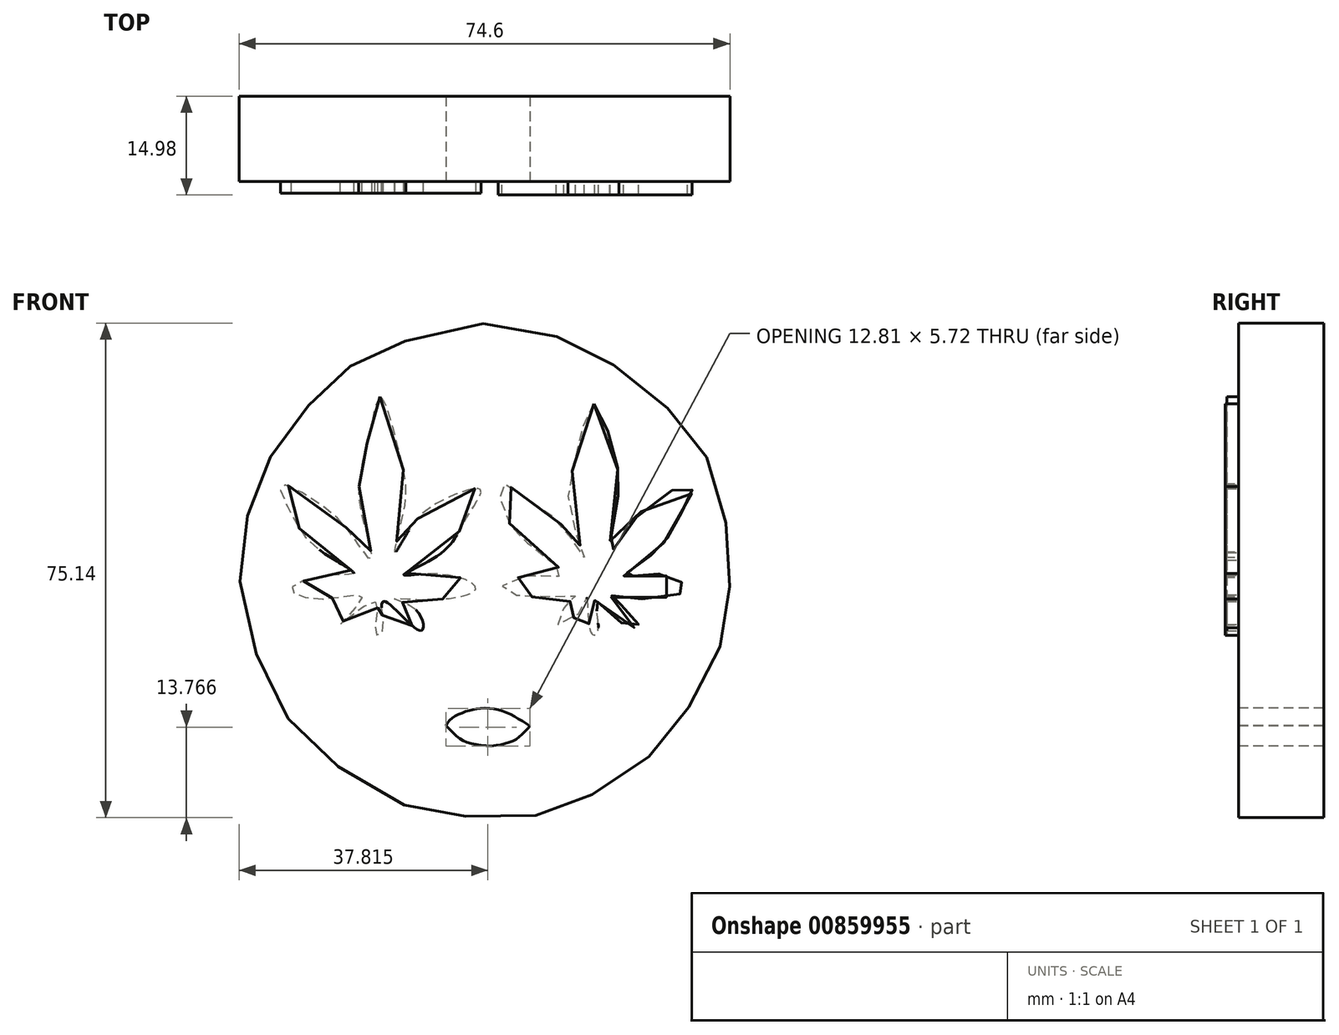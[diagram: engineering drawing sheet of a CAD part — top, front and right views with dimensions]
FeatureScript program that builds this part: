
annotation { "Feature Type Name" : "Feature", "Feature Type Description" : "" }
export const myFeature = defineFeature(function(context is Context, id is Id, definition is map)
    precondition{}
    {
        {
            var Q0;
            Q0=qCreatedBy(makeId("Front.planeOp"),FACE);
            var sketch = newSketch(context, id + "F0", { "sketchPlane" : qUnion([Q0])});
            skFitSpline(sketch, "E0", {"points": [v(-16.7, 29.13) * mm, v(-18.02, 24.43) * mm, v(-18.7, 21.9) * mm, v(-19.39, 19.04) * mm, v(-19.81, 15.55) * mm, v(-19.7, 12.33) * mm, v(-17.93, 4.31) * mm, v(-20.61, 7.65) * mm, v(-24.87, 12.13) * mm, v(-31.65, 15.66) * mm, v(-29.95, 10.92) * mm, v(-26.19, 6.08) * mm, v(-20.59, 2.33) * mm, v(-23.31, 2.06) * mm, v(-30.1, 0) * mm, v(-25.23, -1.6) * mm, v(-19.43, -1.4) * mm, v(-22.7, -5.46) * mm, v(-17.36, -2.02) * mm, v(-17.36, -6.82) * mm, v(-16.34, -6.78) * mm, v(-16.33, -2.15) * mm, v(-14.42, -3.11) * mm, v(-10.37, -6.4) * mm, v(-11, -3.5) * mm, v(-14.47, -1.57) * mm, v(-8.15, -1.69) * mm, v(-2.09, 0) * mm, v(-7.1, 2.12) * mm, v(-13.07, 2.08) * mm, v(-7.55, 5.2) * mm, v(-3.32, 11) * mm, v(-1.42, 15.02) * mm, v(-6.66, 13.63) * mm, v(-11.8, 9.5) * mm, v(-14.39, 5.47) * mm, v(-12.93, 12.38) * mm, v(-13.54, 19.91) * mm, v(-16.7, 29.13) * mm]});
            skSolve(sketch);
        }
        {
            var Q0;
            Q0 = qSketchRegion(id + "F0", true);
            extrude(context, id + "F1", {"entities" : qUnion([Q0]), "depth" : 1.78 * mm, "offsetDistance" : 25.4 * mm});
        }
        {
            var Q0;
            Q0=qCreatedBy(makeId("Front.planeOp"),FACE);
            var sketch = newSketch(context, id + "F2", { "sketchPlane" : qUnion([Q0])});
            skFitSpline(sketch, "E1", {"points": [v(15.82, 28.07) * mm, v(13.17, 20.43) * mm, v(12.15, 11.77) * mm, v(14.35, 4.72) * mm, v(10.97, 9.57) * mm, v(7.15, 12.5) * mm, v(1.57, 15.88) * mm, v(2.6, 10.74) * mm, v(5.54, 7.07) * mm, v(11.27, 2.08) * mm, v(5.83, 1.93) * mm, v(1.87, 0) * mm, v(7.6, -1.3) * mm, v(13.03, -1.15) * mm, v(11.56, -2.62) * mm, v(10.24, -5.41) * mm, v(13.76, -3.5) * mm, v(14.79, -1.45) * mm, v(15.52, -6.88) * mm, v(16.4, -6.59) * mm, v(15.96, -1.6) * mm, v(17.87, -3.8) * mm, v(22.57, -5.85) * mm, v(20.66, -3.06) * mm, v(18.31, -1.15) * mm, v(23.3, -1.6) * mm, v(30.06, 0) * mm, v(27.56, 1.64) * mm, v(23.6, 2.22) * mm, v(20.37, 1.78) * mm, v(23.3, 4.13) * mm, v(26.68, 7.22) * mm, v(29.62, 12.36) * mm, v(30.65, 15.3) * mm, v(23.6, 12.2) * mm, v(18.31, 5.6) * mm, v(19.49, 13.97) * mm, v(19.05, 20) * mm, v(15.82, 28.07) * mm]});
            skSolve(sketch);
        }
        {
            var Q0;
            Q0=makeQuery(id+"F2.imprint","IMPRINT",FACE,{"disambiguationData":[TD([[makeQuery(id+"F2.imprint","IMPRINT",EDGE,{"derivedFrom":sQuery(id+"F2.wireOp",EDGE,"E1")}),1.0]])]});
            extrude(context, id + "F3", {"entities" : qUnion([Q0]), "depth" : 2.03 * mm, "offsetDistance" : 25.4 * mm});
        }
        {
            var Q0;
            Q0=qCreatedBy(makeId("Front.planeOp"),FACE);
            var sketch = newSketch(context, id + "F4", { "sketchPlane" : qUnion([Q0])});
            skFitSpline(sketch, "E2", {"points": [v(-12.89, 37.55) * mm, v(-20.6, 34.19) * mm, v(-25.94, 29.47) * mm, v(-31.94, 22.42) * mm, v(-35.75, 14.17) * mm, v(-38.04, 4.85) * mm, v(-36.44, -6.73) * mm, v(-31.61, -18.3) * mm, v(-24.45, -25.97) * mm, v(-12.97, -32.92) * mm, v(-4.28, -34.6) * mm, v(6.88, -34.5) * mm, v(14.63, -31.8) * mm, v(23.64, -26.06) * mm, v(29.48, -19.18) * mm, v(34.68, -9.87) * mm, v(36.36, -1.24) * mm, v(36.27, 7.3) * mm, v(33.75, 18.17) * mm, v(29.06, 25.31) * mm, v(20.62, 32.75) * mm, v(12.88, 37.1) * mm, v(1.5, 40.28) * mm, v(-12.89, 37.55) * mm]});
            skSolve(sketch);
        }
        {
            var Q0;
            Q0=makeQuery(id+"F4.imprint","IMPRINT",FACE,{"disambiguationData":[TD([[makeQuery(id+"F4.imprint","IMPRINT",EDGE,{"derivedFrom":sQuery(id+"F4.wireOp",EDGE,"E2")}),1.0]])]});
            var sketch = newSketch(context, id + "F5", { "sketchPlane" : qUnion([Q0])});
            skFitSpline(sketch, "E3", {"points": [v(-8.58, -15.32) * mm, v(7.53, -15.56) * mm], "startDerivative": vector(16.1, -0.25) * mm, "endDerivative": vector(16.1, -0.25) * mm});
            skFitSpline(sketch, "E4", {"points": [v(7.53, -15.56) * mm, v(7.53, -16.74) * mm, v(7.53, -18.21) * mm, v(6.14, -20.91) * mm], "startDerivative": vector(-0.16, -4.31) * mm, "endDerivative": vector(-4.22, -6.64) * mm});
            skFitSpline(sketch, "E5", {"points": [v(-8.58, -15.32) * mm, v(-8.58, -17.3) * mm, v(-7.99, -18.7) * mm, v(-6.67, -20.83) * mm], "startDerivative": vector(-0.48, -6.35) * mm, "endDerivative": vector(3.83, -6.02) * mm});
            skFitSpline(sketch, "E6", {"points": [v(-6.67, -20.83) * mm, v(-5.68, -19.67) * mm, v(-3.8, -18.77) * mm, v(-1.84, -18.28) * mm, v(0.96, -18.35) * mm, v(3.57, -19.37) * mm, v(6.14, -20.91) * mm], "startDerivative": vector(6.26, 9.18) * mm, "endDerivative": vector(13.58, -8.6) * mm});
            skFitSpline(sketch, "E7", {"points": [v(6.14, -20.91) * mm, v(5.03, -22.08) * mm, v(3.85, -23) * mm, v(2.25, -23.6) * mm, v(0, -23.93) * mm, v(-2.64, -23.61) * mm, v(-4.42, -22.92) * mm, v(-5.76, -21.73) * mm, v(-6.67, -20.83) * mm], "startDerivative": vector(-9.37, -10.15) * mm, "endDerivative": vector(-8.32, 8.15) * mm});
            skSolve(sketch);
        }
        {
            var Q0;
            Q0=makeQuery(id+"F4.imprint","IMPRINT",FACE,{"disambiguationData":[TD([[makeQuery(id+"F4.imprint","IMPRINT",EDGE,{"derivedFrom":sQuery(id+"F4.wireOp",EDGE,"E2")}),1.0]])]});
            var Q1;
            Q1=sQuery(id+"F4.wireOp",EDGE,"E2");
            extrude(context, id + "F6", {"entities" : qUnion([Q0]), "surfaceEntities" : qUnion([Q1]), "oppositeDirection" : true, "depth" : 12.95 * mm, "offsetDistance" : 25.4 * mm});
        }
        {
            var Q0;
            Q0=makeQuery(id+"F5.imprint","IMPRINT",FACE,{"disambiguationData":[TD([[makeQuery(id+"F5.imprint","IMPRINT",EDGE,{"derivedFrom":sQuery(id+"F5.wireOp",EDGE,"E6")}),-1.0]])]});
            extrude(context, id + "F7", {"entities" : qUnion([Q0]), "operationType" : NewBodyOperationType.REMOVE, "endBound" : BoundingType.THROUGH_ALL, "oppositeDirection" : true, "depth" : 25.4 * mm, "offsetDistance" : 25.4 * mm});
        }
    });
